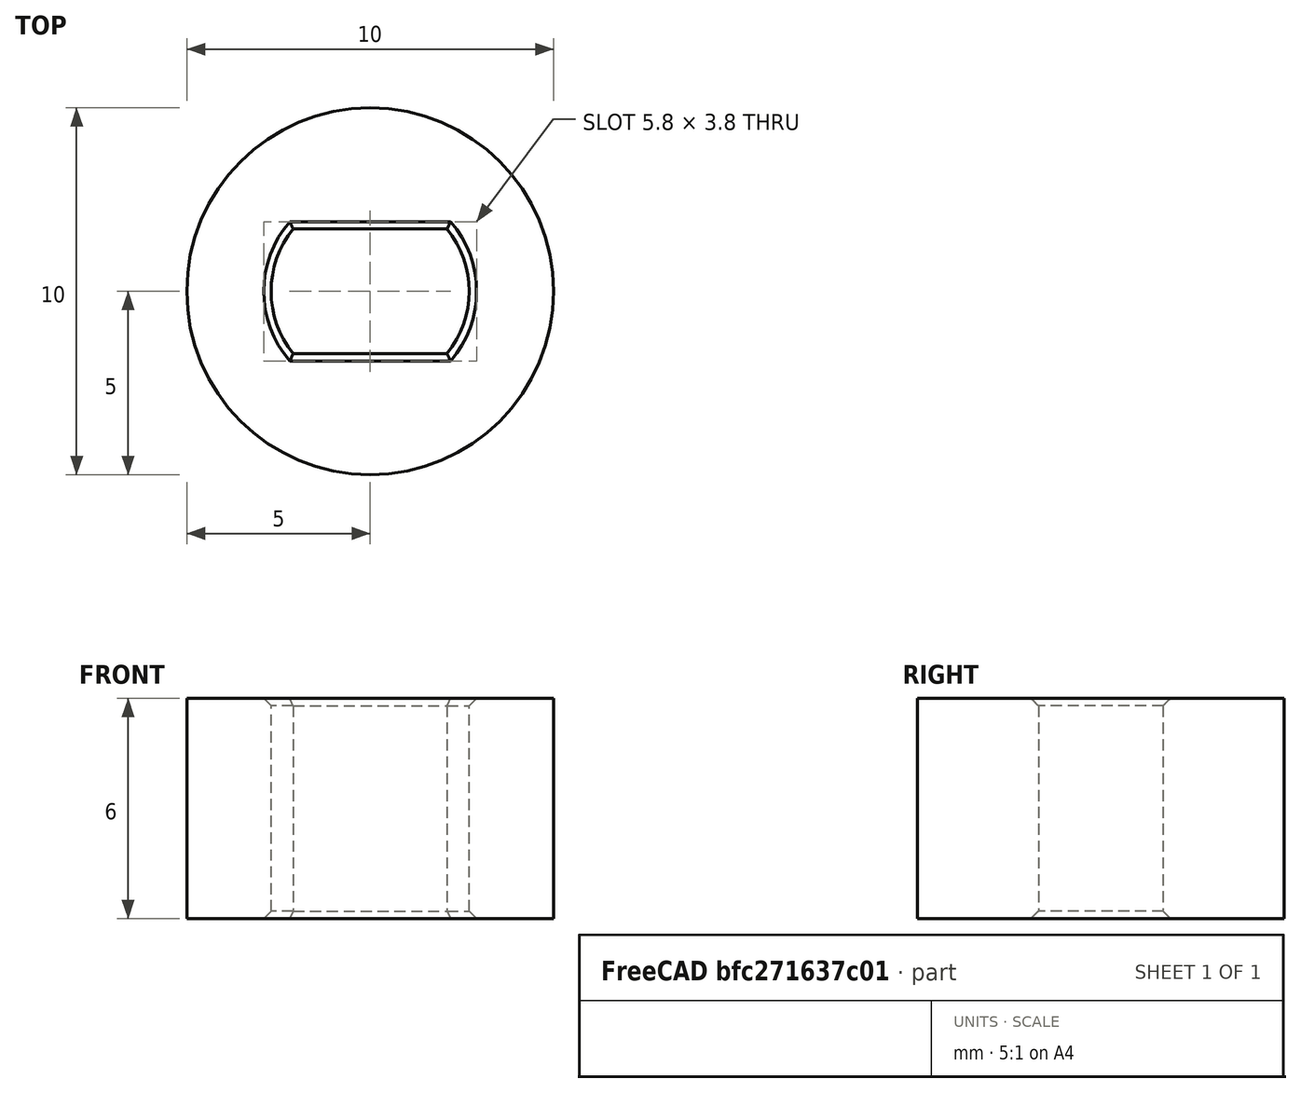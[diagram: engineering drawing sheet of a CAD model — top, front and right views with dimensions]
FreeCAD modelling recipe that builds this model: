
FCSTD DOCUMENT  (FreeCAD 0.18R4 (GitTag))
Label: Stepper_Motor_Connector
License: All rights reserved
LicenseURL: http://en.wikipedia.org/wiki/All_rights_reserved
objects: Sketcher::SketchObject×1, PartDesign::Pad×1, PartDesign::Chamfer×1, PartDesign::Body×1, Mesh::Feature×1
note: 5 computed .brp shape members not serialized (recipe doc carries the construction recipe); baked Part::Feature solids carry a one-line shape summary decoded from their .brp

FEATURE [Sketcher::SketchObject] Sketch
  MapMode = 5
  Support = -> [XY_Plane]
  sketch-geometry (6):
    g0: Circle CenterX=0 CenterY=0 CenterZ=0 NormalX=0 NormalY=0 NormalZ=1 AngleXU=0 Radius=5
    g1: LineSegment StartX=-2.09762 StartY=1.7 StartZ=0 EndX=2.09762 EndY=1.7 EndZ=0
    g2: LineSegment StartX=-2.09762 StartY=-1.7 StartZ=0 EndX=2.09762 EndY=-1.7 EndZ=0
    g3: LineSegment [constr] StartX=0 StartY=-4.81277 StartZ=0 EndX=0 EndY=4.82199 EndZ=0
    g4: ArcOfCircle CenterX=0 CenterY=0 CenterZ=0 NormalX=0 NormalY=0 NormalZ=1 AngleXU=0 Radius=2.7 StartAngle=2.46052 EndAngle=3.82267
    g5: ArcOfCircle CenterX=0 CenterY=0 CenterZ=0 NormalX=0 NormalY=0 NormalZ=1 AngleXU=0 Radius=2.7 StartAngle=5.60211 EndAngle=6.96426
  constraints (15):
    c: Radius(g0) = 5
    c: Parallel(g1,g2)
    c: Horizontal(g1)
    c: Equal(g1,g2)
    c: Coincident(g0,g-1)
    c: Symmetric(g1,g1,g3)
    c: PointOnObject(g0,g3)
    c: DistanceY(g0,g1) = 1.7
    c: Coincident(g4,g1)
    c: Coincident(g4,g2)
    c: Coincident(g4,g0)
    c: Radius(g4) = 2.7
    c: Coincident(g5,g1)
    c: Coincident(g5,g0)
    c: Coincident(g5,g2)
FEATURE [PartDesign::Pad] Pad
  Length = 6
  Length2 = 100
  Profile = -> Sketch
  Reversed = true
  Type = 0
FEATURE [PartDesign::Chamfer] Chamfer
  Base = -> Pad [Edge9,Edge6,Edge14,Edge12,Edge7,Edge15,Edge10,Edge13]
  BaseFeature = -> Pad
  Size = 0.2
FEATURE [PartDesign::Body] Body
  Group = -> [Pad,Sketch,Chamfer]
  Origin = -> Origin
  Tip = -> Chamfer
FEATURE [Mesh::Feature] Mesh  label="Body (Meshed)"
